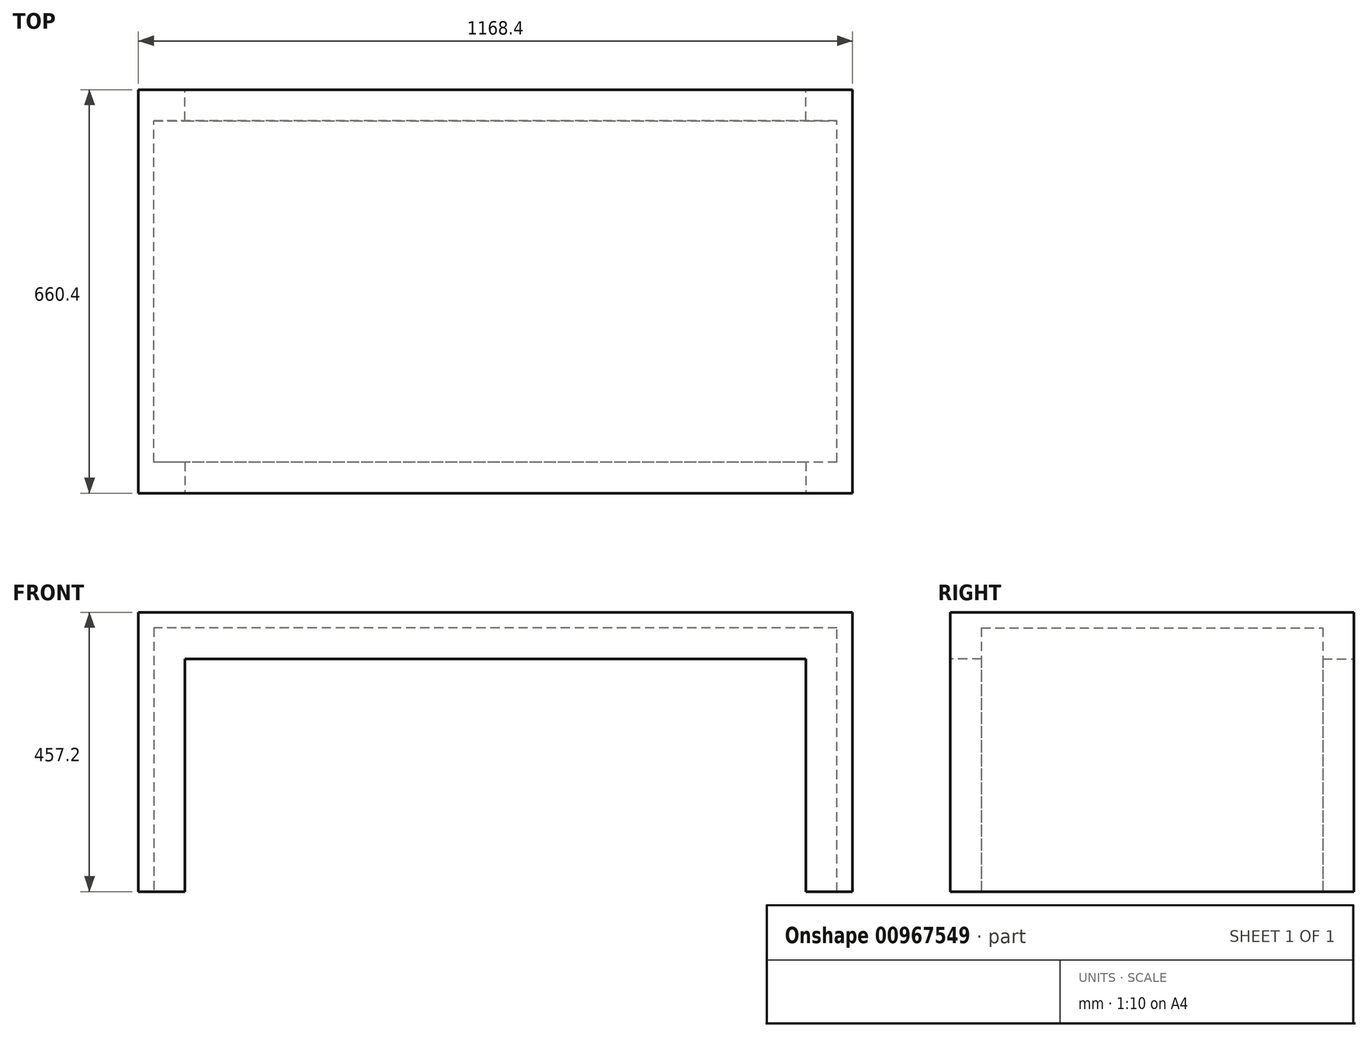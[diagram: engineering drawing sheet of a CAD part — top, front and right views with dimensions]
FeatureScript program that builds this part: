
annotation { "Feature Type Name" : "Feature", "Feature Type Description" : "" }
export const myFeature = defineFeature(function(context is Context, id is Id, definition is map)
    precondition{}
    {
        {
            var Q0;
            Q0=qCreatedBy(makeId("Front.planeOp"),FACE);
            var sketch = newSketch(context, id + "F0", { "sketchPlane" : qUnion([Q0])});
            skLineSegment(sketch, "E0", {"start": v(-584.2, 0) * mm, "end": v(-584.2, 457.2) * mm});
            skLineSegment(sketch, "E1", {"start": v(-584.2, 457.2) * mm, "end": v(584.2, 457.2) * mm});
            skLineSegment(sketch, "E2", {"start": v(584.2, 457.2) * mm, "end": v(584.2, 0) * mm});
            skLineSegment(sketch, "E3", {"start": v(584.2, 0) * mm, "end": v(558.8, 0) * mm});
            skLineSegment(sketch, "E4", {"start": v(558.8, 0) * mm, "end": v(558.8, 431.8) * mm});
            skLineSegment(sketch, "E5", {"start": v(558.8, 431.8) * mm, "end": v(-558.8, 431.8) * mm});
            skLineSegment(sketch, "E6", {"start": v(-558.8, 431.8) * mm, "end": v(-558.8, 0) * mm});
            skLineSegment(sketch, "E7", {"start": v(-558.8, 0) * mm, "end": v(-584.2, 0) * mm});
            skSolve(sketch);
        }
        {
            var Q0;
            Q0=makeQuery(id+"F0.imprint","IMPRINT",FACE,{"disambiguationData":[TD([[makeQuery(id+"F0.imprint","IMPRINT",EDGE,{"derivedFrom":sQuery(id+"F0.wireOp",EDGE,"E0")}),-1.0]])]});
            extrude(context, id + "F1", {"entities" : qUnion([Q0]), "endBound" : BoundingType.SYMMETRIC, "depth" : 660.4 * mm, "offsetDistance" : 25.4 * mm});
        }
        {
            var Q0;
            Q0=makeQuery(id+"F1.opExtrude","CAP_FACE",FACE,{"disambiguationData":[OSD([sQuery(id+"F0.wireOp",EDGE,"E0"),sQuery(id+"F0.wireOp",EDGE,"E1"),sQuery(id+"F0.wireOp",EDGE,"E2"),sQuery(id+"F0.wireOp",EDGE,"E3"),sQuery(id+"F0.wireOp",EDGE,"E4"),sQuery(id+"F0.wireOp",EDGE,"E5"),sQuery(id+"F0.wireOp",EDGE,"E6"),sQuery(id+"F0.wireOp",EDGE,"E7")])],"isStart":false});
            var sketch = newSketch(context, id + "F2", { "sketchPlane" : qUnion([Q0])});
            skLineSegment(sketch, "E8", {"start": v(-584.2, 0) * mm, "end": v(-584.2, 457.2) * mm});
            skLineSegment(sketch, "E9", {"start": v(-584.2, 457.2) * mm, "end": v(584.2, 457.2) * mm});
            skLineSegment(sketch, "E10", {"start": v(584.2, 457.2) * mm, "end": v(584.2, 0) * mm});
            skLineSegment(sketch, "E11", {"start": v(584.2, 0) * mm, "end": v(508, 0) * mm});
            skLineSegment(sketch, "E12", {"start": v(508, 0) * mm, "end": v(508, 381) * mm});
            skLineSegment(sketch, "E13", {"start": v(508, 381) * mm, "end": v(-508, 381) * mm});
            skLineSegment(sketch, "E14", {"start": v(-508, 381) * mm, "end": v(-508, 0) * mm});
            skLineSegment(sketch, "E15", {"start": v(-508, 0) * mm, "end": v(-584.2, 0) * mm});
            skSolve(sketch);
        }
        {
            var Q0;
            {var subQ1=sQuery(id+"F2.wireOp",EDGE,"E12");Q0=makeQuery(id+"F2.imprint","IMPRINT",FACE,{"disambiguationData":[TD([[makeQuery(id+"F2.imprint","IMPRINT",EDGE,{"derivedFrom":subQ1}),-1.0]])]});}
            extrude(context, id + "F3", {"entities" : qUnion([Q0]), "operationType" : NewBodyOperationType.ADD, "oppositeDirection" : true, "depth" : 50.8 * mm, "offsetDistance" : 25.4 * mm});
        }
        {
            var Q0;
            Q0=makeQuery(id+"F1.opExtrude","CAP_FACE",FACE,{"disambiguationData":[OSD([sQuery(id+"F0.wireOp",EDGE,"E0"),sQuery(id+"F0.wireOp",EDGE,"E1"),sQuery(id+"F0.wireOp",EDGE,"E2"),sQuery(id+"F0.wireOp",EDGE,"E3"),sQuery(id+"F0.wireOp",EDGE,"E4"),sQuery(id+"F0.wireOp",EDGE,"E5"),sQuery(id+"F0.wireOp",EDGE,"E6"),sQuery(id+"F0.wireOp",EDGE,"E7")])],"isStart":true});
            var sketch = newSketch(context, id + "F4", { "sketchPlane" : qUnion([Q0])});
            skLineSegment(sketch, "E16", {"start": v(-584.2, 0) * mm, "end": v(-584.2, 457.2) * mm});
            skLineSegment(sketch, "E17", {"start": v(-584.2, 457.2) * mm, "end": v(584.2, 457.2) * mm});
            skLineSegment(sketch, "E18", {"start": v(584.2, 457.2) * mm, "end": v(584.2, 0) * mm});
            skLineSegment(sketch, "E19", {"start": v(584.2, 0) * mm, "end": v(508, 0) * mm});
            skLineSegment(sketch, "E20", {"start": v(508, 0) * mm, "end": v(508, 381) * mm});
            skLineSegment(sketch, "E21", {"start": v(508, 381) * mm, "end": v(-508, 381) * mm});
            skLineSegment(sketch, "E22", {"start": v(-508, 381) * mm, "end": v(-508, 0) * mm});
            skLineSegment(sketch, "E23", {"start": v(-508, 0) * mm, "end": v(-584.2, 0) * mm});
            skSolve(sketch);
        }
        {
            var Q0;
            {var subQ1=sQuery(id+"F4.wireOp",EDGE,"E20");Q0=makeQuery(id+"F4.imprint","IMPRINT",FACE,{"disambiguationData":[TD([[makeQuery(id+"F4.imprint","IMPRINT",EDGE,{"derivedFrom":subQ1}),-1.0]])]});}
            extrude(context, id + "F5", {"entities" : qUnion([Q0]), "operationType" : NewBodyOperationType.ADD, "oppositeDirection" : true, "depth" : 50.8 * mm, "offsetDistance" : 25.4 * mm});
        }
    });
